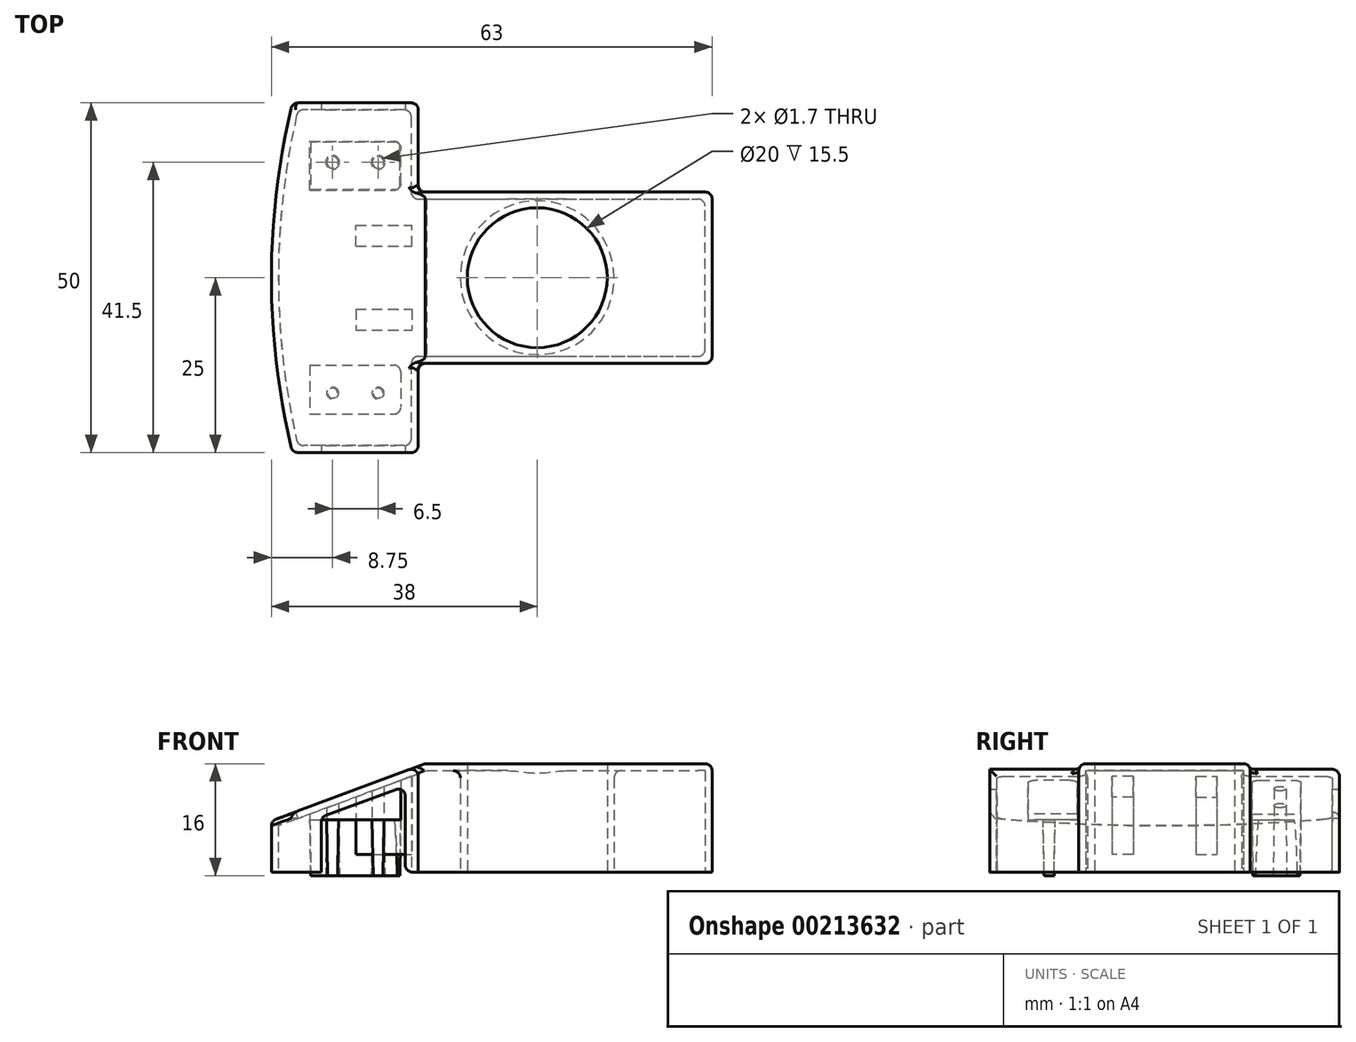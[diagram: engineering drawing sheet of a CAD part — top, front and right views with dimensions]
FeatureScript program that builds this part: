
annotation { "Feature Type Name" : "Feature", "Feature Type Description" : "" }
export const myFeature = defineFeature(function(context is Context, id is Id, definition is map)
    precondition{}
    {
        {
            var Q0;
            Q0=qCreatedBy(makeId("Top.planeOp"),FACE);
            var sketch = newSketch(context, id + "F0", { "sketchPlane" : qUnion([Q0])});
            skCircle(sketch, "E0", {"center": v(-4, 0) * mm, "radius": 10 * mm});
            skLineSegment(sketch, "E1.bottom", {"start": v(-21, -12.25) * mm, "end": v(21, -12.25) * mm});
            skLineSegment(sketch, "E1.top", {"start": v(-21, 12.25) * mm, "end": v(21, 12.25) * mm});
            skLineSegment(sketch, "E1.right", {"start": v(21, -12.25) * mm, "end": v(21, 12.25) * mm});
            skLineSegment(sketch, "E2.bottom", {"start": v(-21, -25) * mm, "end": v(-39, -25) * mm});
            skLineSegment(sketch, "E2.top", {"start": v(-21, 25) * mm, "end": v(-39, 25) * mm});
            skLineSegment(sketch, "E2.left", {"start": v(-21, -25) * mm, "end": v(-21, -12.25) * mm});
            skLineSegment(sketch, "E2.right", {"start": v(-39, -25) * mm, "end": v(-39, 25) * mm});
            skPoint(sketch, "E2.middle", {"position": v(-30, 0) * mm});
            skLineSegment(sketch, "E3.trimOffspring", {"start": v(-21, 12.25) * mm, "end": v(-21, 25) * mm});
            skLineSegment(sketch, "E4", {"start": v(-20, 12.25) * mm, "end": v(-20, -12.25) * mm});
            skPoint(sketch, "E5", {"position": v(-42, 0) * mm});
            skPoint(sketch, "E5.positionSnap0", {"position": v(-39, 0) * mm});
            skArc(sketch, "E6", {"start": v(-39, 25) * mm, "mid": v(-42, 0) * mm, "end": v(-39, -25) * mm});
            skSolve(sketch);
        }
        {
            var Q0;
            Q0 = qSketchRegion(id + "F0", true);
            extrude(context, id + "F1", {"entities" : qUnion([Q0]), "depth" : 15.5 * mm});
        }
        {
            var Q0;
            Q0=makeQuery(id+"F1.opExtrude","SWEPT_FACE",FACE,{"disambiguationData":[OSD([sQuery(id+"F0.wireOp",EDGE,"E2.bottom")])]});
            var sketch = newSketch(context, id + "F2", { "sketchPlane" : qUnion([Q0])});
            skLineSegment(sketch, "E7", {"start": v(-20, 15.5) * mm, "end": v(-42, 7.32) * mm});
            skLineSegment(sketch, "E8", {"start": v(-42, 7.32) * mm, "end": v(-42, 15.5) * mm});
            skLineSegment(sketch, "E9", {"start": v(-42, 15.5) * mm, "end": v(-20, 15.5) * mm});
            skSolve(sketch);
        }
        {
            var Q0;
            {var subQ0=sQuery(id+"F2.wireOp",EDGE,"E8");Q0=makeQuery(id+"F2.imprint","IMPRINT",FACE,{"disambiguationData":[TD([[makeQuery(id+"F2.imprint","IMPRINT",EDGE,{"derivedFrom":subQ0}),1.0]])]});}
            var Q1;
            {var subQ0=sQuery(id+"F2.wireOp",EDGE,"E9");var subQ1=sQuery(id+"F2.wireOp",EDGE,"E7");var subQ2=makeQuery(id+"F2.imprint","INTERSECT",VERTEX,{"derivedFrom":[subQ1,subQ0]});Q1=makeQuery(id+"F2.imprint","IMPRINT",FACE,{"disambiguationData":[TD([[makeQuery(id+"F2.imprint","IMPRINT",EDGE,{"disambiguationData":[TD([[subQ2,-1.0]])],"derivedFrom":subQ1}),-1.0]])]});}
            var Q2;
            {var subQ0=sQuery(id+"F2.wireOp",EDGE,"E8");Q2=makeQuery(id+"F2.imprint","IMPRINT",FACE,{"disambiguationData":[TD([[makeQuery(id+"F2.imprint","IMPRINT",EDGE,{"derivedFrom":subQ0}),-1.0]])]});}
            var Q3;
            {var subQ0=sQuery(id+"F2.wireOp",EDGE,"E7");var subQ1=sQuery(id+"F0.wireOp",EDGE,"E2.bottom");var subQ2=makeQuery(id+"F1.opExtrude","SWEPT_EDGE",EDGE,{"disambiguationData":[OSD([subQ1,sQuery(id+"F0.wireOp",EDGE,"E2.left")])]});var subQ3=makeQuery(id+"F2.imprint","INTERSECT",VERTEX,{"derivedFrom":[subQ2,subQ0]});Q3=makeQuery(id+"F2.imprint","IMPRINT",FACE,{"disambiguationData":[TD([[makeQuery(id+"F2.imprint","IMPRINT",EDGE,{"disambiguationData":[TD([[subQ3,-1.0]])],"derivedFrom":subQ0}),-1.0]])]});}
            extrude(context, id + "F3", {"entities" : qUnion([Q0, Q1, Q2, Q3]), "operationType" : NewBodyOperationType.REMOVE, "endBound" : BoundingType.THROUGH_ALL, "oppositeDirection" : true, "depth" : 25 * mm});
        }
        {
            var Q0;
            {var subQ0=sQuery(id+"F0.wireOp",EDGE,"E1.right");var subQ1=sQuery(id+"F0.wireOp",EDGE,"E1.top");var subQ2=sQuery(id+"F0.wireOp",EDGE,"E1.bottom");var subQ3=sQuery(id+"F0.wireOp",EDGE,"E3.trimOffspring");var subQ4=sQuery(id+"F0.wireOp",EDGE,"E0");var subQ5=sQuery(id+"F0.wireOp",EDGE,"E2.bottom");var subQ6=sQuery(id+"F0.wireOp",EDGE,"E2.top");var subQ7=sQuery(id+"F0.wireOp",EDGE,"E2.left");Q0=makeQuery(id+"F6.boolean.opBoolean","SPLIT",FACE,{"disambiguationData":[TD([makeQuery(id+"F1.opExtrude","SWEPT_FACE",FACE,{"disambiguationData":[OSD([subQ4])]})])],"derivedFrom":makeQuery(id+"F1.opExtrude","CAP_FACE",FACE,{"disambiguationData":[OSD([subQ4,subQ2,subQ1,subQ0,subQ5,subQ6,subQ7,sQuery(id+"F0.wireOp",EDGE,"E2.right"),subQ3])],"isStart":true})});}
            shell(context, id + "F4", {"entities" : qUnion([Q0]), "thickness" : 1 * mm});
        }
        {
            var Q0;
            Q0=makeQuery(id+"F1.opExtrude","SWEPT_FACE",FACE,{"disambiguationData":[OSD([sQuery(id+"F0.wireOp",EDGE,"E2.bottom")])]});
            var sketch = newSketch(context, id + "F5", { "sketchPlane" : qUnion([Q0])});
            skLineSegment(sketch, "E10", {"start": v(-20, 15.5) * mm, "end": v(-39, 8.43) * mm});
            skLineSegment(sketch, "E11", {"start": v(-39, 8.43) * mm, "end": v(-39, 15.5) * mm});
            skLineSegment(sketch, "E12", {"start": v(-39, 15.5) * mm, "end": v(-20, 15.5) * mm});
            skLineSegment(sketch, "E13", {"start": v(-34.87, 0) * mm, "end": v(-34.87, 7.86) * mm});
            skLineSegment(sketch, "E14", {"start": v(-34.87, 7.86) * mm, "end": v(-22.87, 12.32) * mm});
            skLineSegment(sketch, "E15", {"start": v(-22.87, 0) * mm, "end": v(-34.87, 0) * mm});
            skLineSegment(sketch, "E16", {"start": v(-22.87, 12.32) * mm, "end": v(-22.87, 0) * mm});
            skSolve(sketch);
        }
        {
            var Q0;
            Q0=makeQuery(id+"F5.imprint","IMPRINT",FACE,{"disambiguationData":[TD([[makeQuery(id+"F5.imprint","IMPRINT",EDGE,{"derivedFrom":sQuery(id+"F5.wireOp",EDGE,"E13")}),-1.0]])]});
            extrude(context, id + "F6", {"entities" : qUnion([Q0]), "operationType" : NewBodyOperationType.REMOVE, "endBound" : BoundingType.THROUGH_ALL, "oppositeDirection" : true, "depth" : 25 * mm});
        }
        {
            var Q0;
            Q0=makeQuery(id+"F1.opExtrude","CAP_FACE",FACE,{"disambiguationData":[OSD([sQuery(id+"F0.wireOp",EDGE,"E0"),sQuery(id+"F0.wireOp",EDGE,"E1.bottom"),sQuery(id+"F0.wireOp",EDGE,"E1.top"),sQuery(id+"F0.wireOp",EDGE,"E1.right"),sQuery(id+"F0.wireOp",EDGE,"E2.bottom"),sQuery(id+"F0.wireOp",EDGE,"E2.top"),sQuery(id+"F0.wireOp",EDGE,"E2.left"),sQuery(id+"F0.wireOp",EDGE,"E2.right"),sQuery(id+"F0.wireOp",EDGE,"E3.trimOffspring")])],"isStart":false});
            cPlane(context, id + "F7", {"entities" : qUnion([Q0]), "cplaneType" : CPlaneType.OFFSET, "offset" : 8 * mm, "oppositeDirection" : true, "width" : 150 * mm, "height" : 150 * mm});
        }
        {
            var Q0;
            Q0=qCreatedBy(id+"F7.planeOp",FACE);
            var sketch = newSketch(context, id + "F8", { "sketchPlane" : qUnion([Q0])});
            skLineSegment(sketch, "E17", {"start": v(0, 0) * mm, "end": v(-63, 0) * mm, "construction": true});
            skLineSegment(sketch, "E18.bottom", {"start": v(-36.5, -12.5) * mm, "end": v(-23.5, -12.5) * mm});
            skLineSegment(sketch, "E18.top", {"start": v(-36.5, -19.5) * mm, "end": v(-23.5, -19.5) * mm});
            skLineSegment(sketch, "E18.left", {"start": v(-36.5, -12.5) * mm, "end": v(-36.5, -19.5) * mm});
            skLineSegment(sketch, "E18.right", {"start": v(-23.5, -12.5) * mm, "end": v(-23.5, -19.5) * mm});
            skPoint(sketch, "E18.middle", {"position": v(-30, -16) * mm});
            skPoint(sketch, "E19", {"position": v(-33.25, -16.5) * mm});
            skPoint(sketch, "E20", {"position": v(-26.75, -16.5) * mm});
            skCircle(sketch, "E21", {"center": v(-33.25, -16.5) * mm, "radius": 0.85 * mm});
            skCircle(sketch, "E22", {"center": v(-26.75, -16.5) * mm, "radius": 0.85 * mm});
            skLineSegment(sketch, "E23.MirrorCS", {"start": v(-36.5, 12.5) * mm, "end": v(-23.5, 12.5) * mm});
            skLineSegment(sketch, "E24.MirrorCS", {"start": v(-36.5, 12.5) * mm, "end": v(-36.5, 19.5) * mm});
            skLineSegment(sketch, "E25.MirrorCS", {"start": v(-36.5, 19.5) * mm, "end": v(-23.5, 19.5) * mm});
            skLineSegment(sketch, "E26.MirrorCS", {"start": v(-23.5, 12.5) * mm, "end": v(-23.5, 19.5) * mm});
            skCircle(sketch, "E27.MirrorC", {"center": v(-26.75, 16.5) * mm, "radius": 0.85 * mm});
            skCircle(sketch, "E28.MirrorC", {"center": v(-33.25, 16.5) * mm, "radius": 0.85 * mm});
            skSolve(sketch);
        }
        {
            var Q0;
            Q0=makeQuery(id+"F8.imprint","IMPRINT",FACE,{"disambiguationData":[TD([[makeQuery(id+"F8.imprint","IMPRINT",EDGE,{"derivedFrom":sQuery(id+"F8.wireOp",EDGE,"E18.bottom")}),-1.0]])]});
            var Q1;
            Q1=makeQuery(id+"F8.imprint","IMPRINT",FACE,{"disambiguationData":[TD([[makeQuery(id+"F8.imprint","IMPRINT",EDGE,{"derivedFrom":sQuery(id+"F8.wireOp",EDGE,"E21")}),1.0]])]});
            var Q2;
            Q2=makeQuery(id+"F8.imprint","IMPRINT",FACE,{"disambiguationData":[TD([[makeQuery(id+"F8.imprint","IMPRINT",EDGE,{"derivedFrom":sQuery(id+"F8.wireOp",EDGE,"E22")}),1.0]])]});
            var Q3;
            Q3=makeQuery(id+"F8.imprint","IMPRINT",FACE,{"disambiguationData":[TD([[makeQuery(id+"F8.imprint","IMPRINT",EDGE,{"derivedFrom":sQuery(id+"F8.wireOp",EDGE,"E23.MirrorCS")}),1.0]])]});
            var Q4;
            Q4=makeQuery(id+"F8.imprint","IMPRINT",FACE,{"disambiguationData":[TD([[makeQuery(id+"F8.imprint","IMPRINT",EDGE,{"derivedFrom":sQuery(id+"F8.wireOp",EDGE,"E28.MirrorC")}),-1.0]])]});
            var Q5;
            Q5=makeQuery(id+"F8.imprint","IMPRINT",FACE,{"disambiguationData":[TD([[makeQuery(id+"F8.imprint","IMPRINT",EDGE,{"derivedFrom":sQuery(id+"F8.wireOp",EDGE,"E27.MirrorC")}),-1.0]])]});
            var Q6;
            Q6=makeQuery(id+"F4.opShell","OFFSET_FACE",FACE,{"disambiguationData":[OSD([sQuery(id+"F2.wireOp",EDGE,"E7")])]});
            extrude(context, id + "F9", {"entities" : qUnion([Q0, Q1, Q2, Q3, Q4, Q5]), "operationType" : NewBodyOperationType.ADD, "endBound" : BoundingType.UP_TO_SURFACE, "endBoundEntityFace" : qUnion([Q6]), "depth" : 25 * mm});
        }
        {
            var Q0;
            Q0=makeQuery(id+"F8.imprint","IMPRINT",FACE,{"disambiguationData":[TD([[makeQuery(id+"F8.imprint","IMPRINT",EDGE,{"derivedFrom":sQuery(id+"F8.wireOp",EDGE,"E21")}),1.0]])]});
            var Q1;
            Q1=makeQuery(id+"F8.imprint","IMPRINT",FACE,{"disambiguationData":[TD([[makeQuery(id+"F8.imprint","IMPRINT",EDGE,{"derivedFrom":sQuery(id+"F8.wireOp",EDGE,"E27.MirrorC")}),-1.0]])]});
            var Q2;
            Q2=makeQuery(id+"F8.imprint","IMPRINT",FACE,{"disambiguationData":[TD([[makeQuery(id+"F8.imprint","IMPRINT",EDGE,{"derivedFrom":sQuery(id+"F8.wireOp",EDGE,"E28.MirrorC")}),-1.0]])]});
            var Q3;
            Q3=makeQuery(id+"F8.imprint","IMPRINT",FACE,{"disambiguationData":[TD([[makeQuery(id+"F8.imprint","IMPRINT",EDGE,{"derivedFrom":sQuery(id+"F8.wireOp",EDGE,"E22")}),1.0]])]});
            extrude(context, id + "F10", {"entities" : qUnion([Q0, Q1, Q2, Q3]), "operationType" : NewBodyOperationType.ADD, "oppositeDirection" : true, "depth" : 8 * mm, "hasDraft" : true, "draftAngle" : 1 * degree, "draftPullDirection" : true});
        }
        {
            var Q0;
            Q0=makeQuery(id+"F1.opExtrude","CAP_EDGE",EDGE,{"disambiguationData":[OSD([sQuery(id+"F0.wireOp",EDGE,"E1.bottom")])],"isStart":false});
            var Q1;
            Q1=makeQuery(id+"F1.opExtrude","CAP_EDGE",EDGE,{"disambiguationData":[OSD([sQuery(id+"F0.wireOp",EDGE,"E1.right")])],"isStart":false});
            var Q2;
            Q2=makeQuery(id+"F1.opExtrude","CAP_EDGE",EDGE,{"disambiguationData":[OSD([sQuery(id+"F0.wireOp",EDGE,"E1.top")])],"isStart":false});
            var Q3;
            Q3=makeQuery(id+"F1.opExtrude","SWEPT_EDGE",EDGE,{"disambiguationData":[OSD([sQuery(id+"F0.wireOp",EDGE,"E1.bottom"),sQuery(id+"F0.wireOp",EDGE,"E1.right")])]});
            var Q4;
            Q4=makeQuery(id+"F1.opExtrude","SWEPT_EDGE",EDGE,{"disambiguationData":[OSD([sQuery(id+"F0.wireOp",EDGE,"E1.top"),sQuery(id+"F0.wireOp",EDGE,"E1.right")])]});
            fillet(context, id + "F11", {"entities" : qUnion([Q0, Q1, Q2, Q3, Q4]), "radius" : 1 * mm, "tangentPropagation" : true, "allowEdgeOverflow" : false});
        }
        {
            var Q0;
            Q0=makeQuery(id+"F1.opExtrude","SWEPT_EDGE",EDGE,{"disambiguationData":[OSD([sQuery(id+"F0.wireOp",EDGE,"E2.bottom"),sQuery(id+"F0.wireOp",EDGE,"E2.left")])]});
            var Q1;
            Q1=makeQuery(id+"F3.boolean.opBoolean","INTERSECT",EDGE,{"derivedFrom":[makeQuery(id+"F1.opExtrude","SWEPT_FACE",FACE,{"disambiguationData":[OSD([sQuery(id+"F0.wireOp",EDGE,"E2.left")])]}),makeQuery(id+"F3.opExtrude","SWEPT_FACE",FACE,{"disambiguationData":[OSD([sQuery(id+"F2.wireOp",EDGE,"E7")])]})]});
            var Q2;
            Q2=makeQuery(id+"F3.boolean.opBoolean","COPY",EDGE,{"derivedFrom":makeQuery(id+"F3.opExtrude","CAP_EDGE",EDGE,{"disambiguationData":[OSD([sQuery(id+"F2.wireOp",EDGE,"E7")])],"isStart":true})});
            var Q3;
            Q3=makeQuery(id+"F1.opExtrude","SWEPT_EDGE",EDGE,{"disambiguationData":[OSD([sQuery(id+"F0.wireOp",EDGE,"E2.bottom"),sQuery(id+"F0.wireOp",EDGE,"E2.right"),sQuery(id+"F0.wireOp",EDGE,"E6")])]});
            var Q4;
            Q4=makeQuery(id+"F3.boolean.opBoolean","INTERSECT",EDGE,{"derivedFrom":[makeQuery(id+"F1.opExtrude","SWEPT_FACE",FACE,{"disambiguationData":[OSD([sQuery(id+"F0.wireOp",EDGE,"E6")])]}),makeQuery(id+"F3.opExtrude","SWEPT_FACE",FACE,{"disambiguationData":[OSD([sQuery(id+"F2.wireOp",EDGE,"E7")])]})]});
            var Q5;
            Q5=makeQuery(id+"F3.boolean.opBoolean","INTERSECT",EDGE,{"derivedFrom":[makeQuery(id+"F1.opExtrude","SWEPT_FACE",FACE,{"disambiguationData":[OSD([sQuery(id+"F0.wireOp",EDGE,"E2.top")])]}),makeQuery(id+"F3.opExtrude","SWEPT_FACE",FACE,{"disambiguationData":[OSD([sQuery(id+"F2.wireOp",EDGE,"E7")])]})]});
            var Q6;
            Q6=makeQuery(id+"F1.opExtrude","SWEPT_EDGE",EDGE,{"disambiguationData":[OSD([sQuery(id+"F0.wireOp",EDGE,"E2.top"),sQuery(id+"F0.wireOp",EDGE,"E2.right"),sQuery(id+"F0.wireOp",EDGE,"E6")])]});
            var Q7;
            Q7=makeQuery(id+"F1.opExtrude","SWEPT_EDGE",EDGE,{"disambiguationData":[OSD([sQuery(id+"F0.wireOp",EDGE,"E2.top"),sQuery(id+"F0.wireOp",EDGE,"E3.trimOffspring")])]});
            var Q8;
            Q8=makeQuery(id+"F3.boolean.opBoolean","INTERSECT",EDGE,{"derivedFrom":[makeQuery(id+"F1.opExtrude","SWEPT_FACE",FACE,{"disambiguationData":[OSD([sQuery(id+"F0.wireOp",EDGE,"E3.trimOffspring")])]}),makeQuery(id+"F3.opExtrude","SWEPT_FACE",FACE,{"disambiguationData":[OSD([sQuery(id+"F2.wireOp",EDGE,"E7")])]})]});
            fillet(context, id + "F12", {"entities" : qUnion([Q0, Q1, Q2, Q3, Q4, Q5, Q6, Q7, Q8]), "radius" : 1 * mm, "tangentPropagation" : true, "allowEdgeOverflow" : false});
        }
        {
            var Q0;
            Q0=makeQuery(id+"F1.opExtrude","SWEPT_EDGE",EDGE,{"disambiguationData":[OSD([sQuery(id+"F0.wireOp",EDGE,"E1.top"),sQuery(id+"F0.wireOp",EDGE,"E3.trimOffspring")])]});
            fillet(context, id + "F13", {"entities" : qUnion([Q0]), "radius" : 1 * mm, "tangentPropagation" : true, "allowEdgeOverflow" : false});
        }
        {
            var Q0;
            Q0=makeQuery(id+"F1.opExtrude","SWEPT_EDGE",EDGE,{"disambiguationData":[OSD([sQuery(id+"F0.wireOp",EDGE,"E1.bottom"),sQuery(id+"F0.wireOp",EDGE,"E2.left")])]});
            var Q1;
            {var subQ0=sQuery(id+"F0.wireOp",EDGE,"E2.bottom");var subQ1=sQuery(id+"F5.wireOp",EDGE,"E16");Q1=makeQuery(id+"F6.boolean.opBoolean","COPY",EDGE,{"disambiguationData":[TD([makeQuery(id+"F1.opExtrude","SWEPT_FACE",FACE,{"disambiguationData":[OSD([subQ0])]})])],"derivedFrom":makeQuery(id+"F6.opExtrude","SWEPT_EDGE",EDGE,{"disambiguationData":[OSD([subQ0,sQuery(id+"F5.wireOp",EDGE,"E15"),subQ1])]})});}
            var Q2;
            {var subQ0=sQuery(id+"F0.wireOp",EDGE,"E2.bottom");var subQ1=sQuery(id+"F5.wireOp",EDGE,"E13");Q2=makeQuery(id+"F6.boolean.opBoolean","COPY",EDGE,{"disambiguationData":[TD([makeQuery(id+"F1.opExtrude","SWEPT_FACE",FACE,{"disambiguationData":[OSD([subQ0])]})])],"derivedFrom":makeQuery(id+"F6.opExtrude","SWEPT_EDGE",EDGE,{"disambiguationData":[OSD([subQ0,subQ1,sQuery(id+"F5.wireOp",EDGE,"E15")])]})});}
            var Q3;
            {var subQ0=sQuery(id+"F0.wireOp",EDGE,"E2.top");var subQ1=sQuery(id+"F0.wireOp",EDGE,"E2.bottom");var subQ2=sQuery(id+"F5.wireOp",EDGE,"E13");Q3=makeQuery(id+"F6.boolean.opBoolean","COPY",EDGE,{"disambiguationData":[TD([makeQuery(id+"F1.opExtrude","SWEPT_FACE",FACE,{"disambiguationData":[OSD([subQ0])]})])],"derivedFrom":makeQuery(id+"F6.opExtrude","SWEPT_EDGE",EDGE,{"disambiguationData":[OSD([subQ1,subQ2,sQuery(id+"F5.wireOp",EDGE,"E15")])]})});}
            var Q4;
            {var subQ0=sQuery(id+"F0.wireOp",EDGE,"E2.top");var subQ1=sQuery(id+"F0.wireOp",EDGE,"E2.bottom");var subQ2=sQuery(id+"F5.wireOp",EDGE,"E16");Q4=makeQuery(id+"F6.boolean.opBoolean","COPY",EDGE,{"disambiguationData":[TD([makeQuery(id+"F1.opExtrude","SWEPT_FACE",FACE,{"disambiguationData":[OSD([subQ0])]})])],"derivedFrom":makeQuery(id+"F6.opExtrude","SWEPT_EDGE",EDGE,{"disambiguationData":[OSD([subQ1,sQuery(id+"F5.wireOp",EDGE,"E15"),subQ2])]})});}
            var Q5;
            {var subQ0=sQuery(id+"F0.wireOp",EDGE,"E2.top");var subQ1=sQuery(id+"F5.wireOp",EDGE,"E16");var subQ2=sQuery(id+"F5.wireOp",EDGE,"E14");Q5=makeQuery(id+"F6.boolean.opBoolean","COPY",EDGE,{"disambiguationData":[TD([makeQuery(id+"F1.opExtrude","SWEPT_FACE",FACE,{"disambiguationData":[OSD([subQ0])]})])],"derivedFrom":makeQuery(id+"F6.opExtrude","SWEPT_EDGE",EDGE,{"disambiguationData":[OSD([subQ2,subQ1])]})});}
            var Q6;
            {var subQ0=sQuery(id+"F0.wireOp",EDGE,"E2.top");var subQ1=sQuery(id+"F5.wireOp",EDGE,"E13");var subQ2=sQuery(id+"F5.wireOp",EDGE,"E14");Q6=makeQuery(id+"F6.boolean.opBoolean","COPY",EDGE,{"disambiguationData":[TD([makeQuery(id+"F1.opExtrude","SWEPT_FACE",FACE,{"disambiguationData":[OSD([subQ0])]})])],"derivedFrom":makeQuery(id+"F6.opExtrude","SWEPT_EDGE",EDGE,{"disambiguationData":[OSD([subQ1,subQ2])]})});}
            var Q7;
            {var subQ0=sQuery(id+"F0.wireOp",EDGE,"E2.bottom");var subQ1=sQuery(id+"F5.wireOp",EDGE,"E16");var subQ2=sQuery(id+"F5.wireOp",EDGE,"E14");Q7=makeQuery(id+"F6.boolean.opBoolean","COPY",EDGE,{"disambiguationData":[TD([makeQuery(id+"F1.opExtrude","SWEPT_FACE",FACE,{"disambiguationData":[OSD([subQ0])]})])],"derivedFrom":makeQuery(id+"F6.opExtrude","SWEPT_EDGE",EDGE,{"disambiguationData":[OSD([subQ2,subQ1])]})});}
            var Q8;
            {var subQ0=sQuery(id+"F0.wireOp",EDGE,"E2.bottom");var subQ1=sQuery(id+"F5.wireOp",EDGE,"E13");var subQ2=sQuery(id+"F5.wireOp",EDGE,"E14");Q8=makeQuery(id+"F6.boolean.opBoolean","COPY",EDGE,{"disambiguationData":[TD([makeQuery(id+"F1.opExtrude","SWEPT_FACE",FACE,{"disambiguationData":[OSD([subQ0])]})])],"derivedFrom":makeQuery(id+"F6.opExtrude","SWEPT_EDGE",EDGE,{"disambiguationData":[OSD([subQ1,subQ2])]})});}
            var Q9;
            Q9=makeQuery(id+"F4.opShell","OFFSET_EDGE",EDGE,{"disambiguationData":[OSD([sQuery(id+"F0.wireOp",EDGE,"E1.top"),sQuery(id+"F0.wireOp",EDGE,"E3.trimOffspring")])]});
            var Q10;
            Q10=makeQuery(id+"F4.opShell","OFFSET_EDGE",EDGE,{"disambiguationData":[OSD([sQuery(id+"F0.wireOp",EDGE,"E1.bottom"),sQuery(id+"F0.wireOp",EDGE,"E2.left")])]});
            fillet(context, id + "F14", {"entities" : qUnion([Q0, Q1, Q2, Q3, Q4, Q5, Q6, Q7, Q8, Q9, Q10]), "radius" : 1 * mm, "tangentPropagation" : true, "allowEdgeOverflow" : false});
        }
        {
            var Q0;
            Q0=makeQuery(id+"F4.opShell","OFFSET_EDGE",EDGE,{"disambiguationData":[OSD([sQuery(id+"F0.wireOp",EDGE,"E1.top"),sQuery(id+"F0.wireOp",EDGE,"E1.right")])]});
            var Q1;
            Q1=makeQuery(id+"F4.opShell","OFFSET_EDGE",EDGE,{"disambiguationData":[OSD([sQuery(id+"F0.wireOp",EDGE,"E1.bottom"),sQuery(id+"F0.wireOp",EDGE,"E1.right")])]});
            var Q2;
            {var subQ0=sQuery(id+"F0.wireOp",EDGE,"E0");Q2=makeQuery(id+"F4.opShell","OFFSET_EDGE",EDGE,{"disambiguationData":[OSD([subQ0]),TDD([makeQuery(id+"F1.opExtrude","CAP_EDGE",EDGE,{"disambiguationData":[OSD([subQ0])],"isStart":false})])]});}
            var Q3;
            Q3=makeQuery(id+"F4.opShell","OFFSET_EDGE",EDGE,{"disambiguationData":[OSD([sQuery(id+"F0.wireOp",EDGE,"E2.top"),sQuery(id+"F0.wireOp",EDGE,"E3.trimOffspring")])]});
            var Q4;
            Q4=makeQuery(id+"F4.opShell","OFFSET_EDGE",EDGE,{"disambiguationData":[OSD([sQuery(id+"F0.wireOp",EDGE,"E2.top"),sQuery(id+"F0.wireOp",EDGE,"E2.right"),sQuery(id+"F0.wireOp",EDGE,"E6")])]});
            var Q5;
            Q5=makeQuery(id+"F4.opShell","OFFSET_EDGE",EDGE,{"disambiguationData":[OSD([sQuery(id+"F0.wireOp",EDGE,"E2.bottom"),sQuery(id+"F0.wireOp",EDGE,"E2.left")])]});
            var Q6;
            Q6=makeQuery(id+"F4.opShell","OFFSET_EDGE",EDGE,{"disambiguationData":[OSD([sQuery(id+"F0.wireOp",EDGE,"E2.bottom"),sQuery(id+"F0.wireOp",EDGE,"E2.right"),sQuery(id+"F0.wireOp",EDGE,"E6")])]});
            var Q7;
            Q7=makeQuery(id+"F9.opExtrude","SWEPT_EDGE",EDGE,{"disambiguationData":[OSD([sQuery(id+"F8.wireOp",EDGE,"E18.bottom"),sQuery(id+"F8.wireOp",EDGE,"E18.right")])]});
            var Q8;
            Q8=makeQuery(id+"F9.opExtrude","SWEPT_EDGE",EDGE,{"disambiguationData":[OSD([sQuery(id+"F8.wireOp",EDGE,"E18.top"),sQuery(id+"F8.wireOp",EDGE,"E18.right")])]});
            var Q9;
            Q9=makeQuery(id+"F9.opExtrude","SWEPT_EDGE",EDGE,{"disambiguationData":[OSD([sQuery(id+"F8.wireOp",EDGE,"E25.MirrorCS"),sQuery(id+"F8.wireOp",EDGE,"E26.MirrorCS")])]});
            var Q10;
            Q10=makeQuery(id+"F9.opExtrude","SWEPT_EDGE",EDGE,{"disambiguationData":[OSD([sQuery(id+"F8.wireOp",EDGE,"E23.MirrorCS"),sQuery(id+"F8.wireOp",EDGE,"E26.MirrorCS")])]});
            fillet(context, id + "F15", {"entities" : qUnion([Q0, Q1, Q2, Q3, Q4, Q5, Q6, Q7, Q8, Q9, Q10]), "radius" : 1 * mm, "tangentPropagation" : true, "allowEdgeOverflow" : false});
        }
        {
            var Q0;
            Q0=qCreatedBy(id+"F7.planeOp",FACE);
            var sketch = newSketch(context, id + "F16", { "sketchPlane" : qUnion([Q0])});
            skPoint(sketch, "E29", {"position": v(-29.94, -4.5) * mm});
            skLineSegment(sketch, "E30.bottom", {"start": v(-29.94, -4.5) * mm, "end": v(-21.94, -4.5) * mm});
            skLineSegment(sketch, "E30.top", {"start": v(-29.94, -7.5) * mm, "end": v(-21.94, -7.5) * mm});
            skLineSegment(sketch, "E30.left", {"start": v(-29.94, -4.5) * mm, "end": v(-29.94, -7.5) * mm});
            skLineSegment(sketch, "E30.right", {"start": v(-21.94, -4.5) * mm, "end": v(-21.94, -7.5) * mm});
            skLineSegment(sketch, "E31", {"start": v(0, 0) * mm, "end": v(-48.4, 0) * mm, "construction": true});
            skLineSegment(sketch, "E32.MirrorCS", {"start": v(-29.94, 4.5) * mm, "end": v(-21.94, 4.5) * mm});
            skLineSegment(sketch, "E33.MirrorCS", {"start": v(-21.94, 4.5) * mm, "end": v(-21.94, 7.5) * mm});
            skLineSegment(sketch, "E34.MirrorCS", {"start": v(-29.94, 7.5) * mm, "end": v(-21.94, 7.5) * mm});
            skLineSegment(sketch, "E35.MirrorCS", {"start": v(-29.94, 4.5) * mm, "end": v(-29.94, 7.5) * mm});
            skSolve(sketch);
        }
        {
            var Q0;
            Q0 = qSketchRegion(id + "F16", true);
            var Q1;
            Q1=makeQuery(id+"F4.opShell","OFFSET_FACE",FACE,{"disambiguationData":[OSD([sQuery(id+"F2.wireOp",EDGE,"E7")])]});
            extrude(context, id + "F17", {"entities" : qUnion([Q0]), "operationType" : NewBodyOperationType.ADD, "endBound" : BoundingType.UP_TO_SURFACE, "endBoundEntityFace" : qUnion([Q1]), "depth" : 25 * mm, "hasSecondDirection" : true, "secondDirectionOppositeDirection" : true, "secondDirectionDepth" : 5 * mm});
        }
    });
